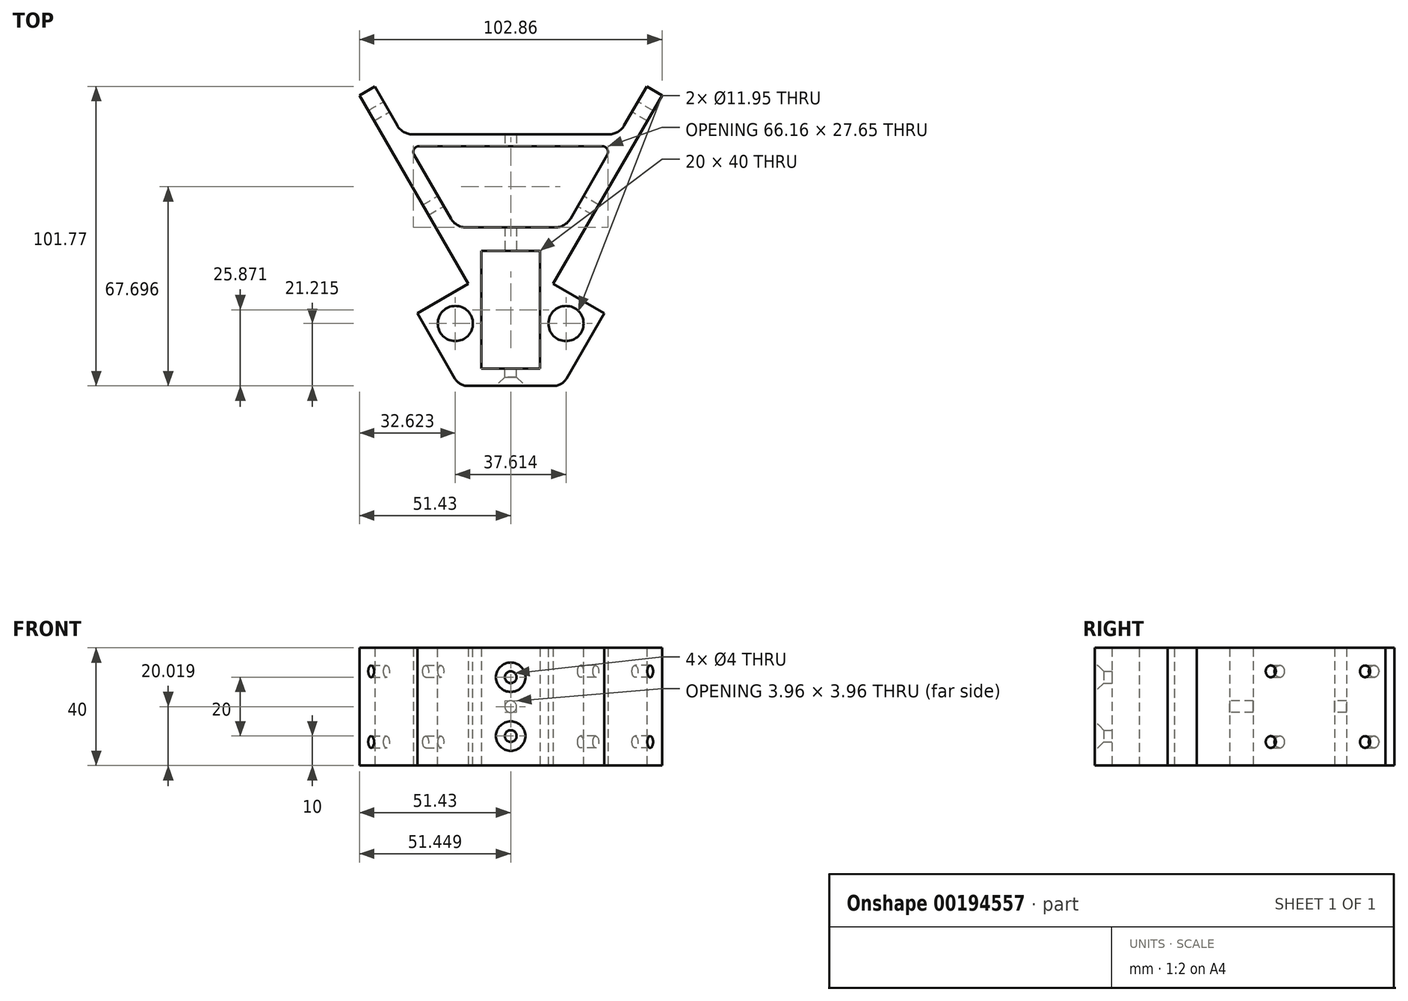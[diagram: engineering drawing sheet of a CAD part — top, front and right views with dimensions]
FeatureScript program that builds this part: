
annotation { "Feature Type Name" : "Feature", "Feature Type Description" : "" }
export const myFeature = defineFeature(function(context is Context, id is Id, definition is map)
    precondition{}
    {
        {
            var Q0;
            Q0=qCreatedBy(makeId("Top.planeOp"),FACE);
            var sketch = newSketch(context, id + "F0", { "sketchPlane" : qUnion([Q0])});
            skLineSegment(sketch, "E0", {"start": v(17.5, 30.31) * mm, "end": v(31.75, 55) * mm});
            skLineSegment(sketch, "E1", {"start": v(-17.5, 30.31) * mm, "end": v(-31.75, 55) * mm});
            skLineSegment(sketch, "E2", {"start": v(-17.5, 30.31) * mm, "end": v(17.5, 30.31) * mm});
            skLineSegment(sketch, "E3", {"start": v(-31.75, 55) * mm, "end": v(-14.43, 65) * mm});
            skLineSegment(sketch, "E4", {"start": v(-14.43, 65) * mm, "end": v(-51.43, 129.08) * mm});
            skLineSegment(sketch, "E5", {"start": v(-51.43, 129.08) * mm, "end": v(-46.23, 132.08) * mm});
            skLineSegment(sketch, "E6", {"start": v(31.75, 55) * mm, "end": v(14.43, 65) * mm});
            skLineSegment(sketch, "E7", {"start": v(14.43, 65) * mm, "end": v(51.43, 129.08) * mm});
            skLineSegment(sketch, "E8", {"start": v(51.43, 129.08) * mm, "end": v(46.23, 132.08) * mm});
            skLineSegment(sketch, "E9", {"start": v(-46.23, 132.08) * mm, "end": v(-36.85, 115.83) * mm});
            skLineSegment(sketch, "E10", {"start": v(18.58, 84.18) * mm, "end": v(34.54, 111.83) * mm});
            skLineSegment(sketch, "E11.bottom", {"start": v(-10, 36.18) * mm, "end": v(10, 36.18) * mm});
            skLineSegment(sketch, "E11.top", {"start": v(-10, 76.18) * mm, "end": v(10, 76.18) * mm});
            skLineSegment(sketch, "E11.left", {"start": v(-10, 36.18) * mm, "end": v(-10, 76.18) * mm});
            skLineSegment(sketch, "E11.right", {"start": v(10, 36.18) * mm, "end": v(10, 76.18) * mm});
            skLineSegment(sketch, "E12", {"start": v(36.85, 115.83) * mm, "end": v(-36.85, 115.83) * mm});
            skLineSegment(sketch, "E13.trimOffspring", {"start": v(36.85, 115.83) * mm, "end": v(46.23, 132.08) * mm});
            skLineSegment(sketch, "E14.trimOffspring", {"start": v(-34.54, 111.83) * mm, "end": v(-18.58, 84.18) * mm});
            skLineSegment(sketch, "E15", {"start": v(-34.54, 111.83) * mm, "end": v(34.54, 111.83) * mm});
            skLineSegment(sketch, "E16", {"start": v(18.58, 84.18) * mm, "end": v(-18.58, 84.18) * mm});
            skSolve(sketch);
        }
        {
            var Q0;
            Q0=qSketchRegion(id+"F0",true);
            extrude(context, id + "F1", {"entities" : qUnion([Q0]), "depth" : 40 * mm});
        }
        {
            var Q0;
            Q0=makeQuery(id+"F1.opExtrude","SWEPT_EDGE",EDGE,{"disambiguationData":[OSD([sQuery(id+"F0.wireOp",EDGE,"E1"),sQuery(id+"F0.wireOp",EDGE,"E2")])]});
            var Q1;
            Q1=makeQuery(id+"F1.opExtrude","SWEPT_EDGE",EDGE,{"disambiguationData":[OSD([sQuery(id+"F0.wireOp",EDGE,"E0"),sQuery(id+"F0.wireOp",EDGE,"E2")])]});
            fillet(context, id + "F2", {"entities" : qUnion([Q0, Q1]), "radius" : 5 * mm, "tangentPropagation" : true, "allowEdgeOverflow" : false});
        }
        {
            var Q0;
            Q0=makeQuery(id+"F1.opExtrude","SWEPT_EDGE",EDGE,{"disambiguationData":[OSD([sQuery(id+"F0.wireOp",EDGE,"E10"),sQuery(id+"F0.wireOp",EDGE,"E16")])]});
            var Q1;
            Q1=makeQuery(id+"F1.opExtrude","SWEPT_EDGE",EDGE,{"disambiguationData":[OSD([sQuery(id+"F0.wireOp",EDGE,"E14.trimOffspring"),sQuery(id+"F0.wireOp",EDGE,"E16")])]});
            var Q2;
            Q2=makeQuery(id+"F1.opExtrude","SWEPT_EDGE",EDGE,{"disambiguationData":[OSD([sQuery(id+"F0.wireOp",EDGE,"E9"),sQuery(id+"F0.wireOp",EDGE,"E12")])]});
            var Q3;
            Q3=makeQuery(id+"F1.opExtrude","SWEPT_EDGE",EDGE,{"disambiguationData":[OSD([sQuery(id+"F0.wireOp",EDGE,"E12"),sQuery(id+"F0.wireOp",EDGE,"E13.trimOffspring")])]});
            fillet(context, id + "F3", {"entities" : qUnion([Q0, Q1, Q2, Q3]), "radius" : 6 * mm, "tangentPropagation" : true, "allowEdgeOverflow" : false});
        }
        {
            var Q0;
            Q0=makeQuery(id+"F1.opExtrude","SWEPT_EDGE",EDGE,{"disambiguationData":[OSD([sQuery(id+"F0.wireOp",EDGE,"E10"),sQuery(id+"F0.wireOp",EDGE,"E15")])]});
            var Q1;
            Q1=makeQuery(id+"F1.opExtrude","SWEPT_EDGE",EDGE,{"disambiguationData":[OSD([sQuery(id+"F0.wireOp",EDGE,"E14.trimOffspring"),sQuery(id+"F0.wireOp",EDGE,"E15")])]});
            fillet(context, id + "F4", {"entities" : qUnion([Q0, Q1]), "radius" : 2 * mm, "tangentPropagation" : true, "allowEdgeOverflow" : false});
        }
        {
            var Q0;
            Q0=makeQuery(id+"F1.opExtrude","CAP_FACE",FACE,{"disambiguationData":[OSD([sQuery(id+"F0.wireOp",EDGE,"E0"),sQuery(id+"F0.wireOp",EDGE,"E1"),sQuery(id+"F0.wireOp",EDGE,"E2"),sQuery(id+"F0.wireOp",EDGE,"E3"),sQuery(id+"F0.wireOp",EDGE,"E4"),sQuery(id+"F0.wireOp",EDGE,"E5"),sQuery(id+"F0.wireOp",EDGE,"E6"),sQuery(id+"F0.wireOp",EDGE,"E7"),sQuery(id+"F0.wireOp",EDGE,"E8"),sQuery(id+"F0.wireOp",EDGE,"E9"),sQuery(id+"F0.wireOp",EDGE,"E10"),sQuery(id+"F0.wireOp",EDGE,"E11.bottom"),sQuery(id+"F0.wireOp",EDGE,"E11.top"),sQuery(id+"F0.wireOp",EDGE,"E11.left"),sQuery(id+"F0.wireOp",EDGE,"E11.right"),sQuery(id+"F0.wireOp",EDGE,"E12"),sQuery(id+"F0.wireOp",EDGE,"E13.trimOffspring"),sQuery(id+"F0.wireOp",EDGE,"E14.trimOffspring"),sQuery(id+"F0.wireOp",EDGE,"E15"),sQuery(id+"F0.wireOp",EDGE,"E16")])],"isStart":false});
            var sketch = newSketch(context, id + "F5", { "sketchPlane" : qUnion([Q0])});
            skCircle(sketch, "E17", {"center": v(-18.8, 51.52) * mm, "radius": 5.97 * mm});
            skCircle(sketch, "E18", {"center": v(18.8, 51.52) * mm, "radius": 5.97 * mm});
            skSolve(sketch);
        }
        {
            var Q0;
            Q0=qSketchRegion(id+"F5",true);
            extrude(context, id + "F6", {"entities" : qUnion([Q0]), "operationType" : NewBodyOperationType.REMOVE, "endBound" : BoundingType.THROUGH_ALL, "oppositeDirection" : true, "depth" : 25 * mm});
        }
        {
            var Q0;
            Q0=makeQuery(id+"F1.opExtrude","SWEPT_FACE",FACE,{"disambiguationData":[OSD([sQuery(id+"F0.wireOp",EDGE,"E12")])]});
            var sketch = newSketch(context, id + "F7", { "sketchPlane" : qUnion([Q0])});
            skPoint(sketch, "E19", {"position": v(0, 20) * mm});
            skPoint(sketch, "E19.positionSnap0", {"position": v(-33.39, 20) * mm});
            skSolve(sketch);
        }
        {
            var Q0;
            Q0=sQuery(id+"F7.wireOp",VERTEX,"E19");
            var Q1;
            Q1=makeQuery(id+"F1.opExtrude","SWEPT_BODY",BODY,{"disambiguationData":[OSD([sQuery(id+"F0.wireOp",EDGE,"E0"),sQuery(id+"F0.wireOp",EDGE,"E1"),sQuery(id+"F0.wireOp",EDGE,"E2"),sQuery(id+"F0.wireOp",EDGE,"E3"),sQuery(id+"F0.wireOp",EDGE,"E4"),sQuery(id+"F0.wireOp",EDGE,"E5"),sQuery(id+"F0.wireOp",EDGE,"E6"),sQuery(id+"F0.wireOp",EDGE,"E7"),sQuery(id+"F0.wireOp",EDGE,"E8"),sQuery(id+"F0.wireOp",EDGE,"E9"),sQuery(id+"F0.wireOp",EDGE,"E10"),sQuery(id+"F0.wireOp",EDGE,"E11.bottom"),sQuery(id+"F0.wireOp",EDGE,"E11.top"),sQuery(id+"F0.wireOp",EDGE,"E11.left"),sQuery(id+"F0.wireOp",EDGE,"E11.right"),sQuery(id+"F0.wireOp",EDGE,"E12"),sQuery(id+"F0.wireOp",EDGE,"E13.trimOffspring"),sQuery(id+"F0.wireOp",EDGE,"E14.trimOffspring"),sQuery(id+"F0.wireOp",EDGE,"E15"),sQuery(id+"F0.wireOp",EDGE,"E16")])]});
            hole(context, id + "F8", {"style" : HoleStyle.SIMPLE, "endStyle" : HoleEndStyle.BLIND, "holeDiameter" : 4 * mm, "holeDepth" : 40 * mm, "locations" : qUnion([Q0]), "scope" : qUnion([Q1]), "startStyle" : HoleStartStyle.PART});
        }
        {
            var Q0;
            Q0=makeQuery(id+"F1.opExtrude","SWEPT_FACE",FACE,{"disambiguationData":[OSD([sQuery(id+"F0.wireOp",EDGE,"E7")])]});
            var sketch = newSketch(context, id + "F9", { "sketchPlane" : qUnion([Q0])});
            skPoint(sketch, "E20", {"position": v(129.5, 32) * mm});
            skPoint(sketch, "E21", {"position": v(129.5, 8) * mm});
            skPoint(sketch, "E22", {"position": v(92.5, 8) * mm});
            skPoint(sketch, "E23", {"position": v(92.5, 32) * mm});
            skSolve(sketch);
        }
        {
            var Q0;
            Q0=sQuery(id+"F9.wireOp",VERTEX,"E20");
            var Q1;
            Q1=sQuery(id+"F9.wireOp",VERTEX,"E23");
            var Q2;
            Q2=sQuery(id+"F9.wireOp",VERTEX,"E22");
            var Q3;
            Q3=sQuery(id+"F9.wireOp",VERTEX,"E21");
            var Q4;
            Q4=makeQuery(id+"F1.opExtrude","SWEPT_BODY",BODY,{"disambiguationData":[OSD([sQuery(id+"F0.wireOp",EDGE,"E0"),sQuery(id+"F0.wireOp",EDGE,"E1"),sQuery(id+"F0.wireOp",EDGE,"E2"),sQuery(id+"F0.wireOp",EDGE,"E3"),sQuery(id+"F0.wireOp",EDGE,"E4"),sQuery(id+"F0.wireOp",EDGE,"E5"),sQuery(id+"F0.wireOp",EDGE,"E6"),sQuery(id+"F0.wireOp",EDGE,"E7"),sQuery(id+"F0.wireOp",EDGE,"E8"),sQuery(id+"F0.wireOp",EDGE,"E9"),sQuery(id+"F0.wireOp",EDGE,"E10"),sQuery(id+"F0.wireOp",EDGE,"E11.bottom"),sQuery(id+"F0.wireOp",EDGE,"E11.top"),sQuery(id+"F0.wireOp",EDGE,"E11.left"),sQuery(id+"F0.wireOp",EDGE,"E11.right"),sQuery(id+"F0.wireOp",EDGE,"E12"),sQuery(id+"F0.wireOp",EDGE,"E13.trimOffspring"),sQuery(id+"F0.wireOp",EDGE,"E14.trimOffspring"),sQuery(id+"F0.wireOp",EDGE,"E15"),sQuery(id+"F0.wireOp",EDGE,"E16")])]});
            hole(context, id + "F10", {"style" : HoleStyle.SIMPLE, "endStyle" : HoleEndStyle.BLIND, "holeDiameter" : 4 * mm, "holeDepth" : 12 * mm, "locations" : qUnion([Q0, Q1, Q2, Q3]), "scope" : qUnion([Q4]), "startStyle" : HoleStartStyle.PART});
        }
        {
            var Q0;
            Q0=makeQuery(id+"F1.opExtrude","SWEPT_FACE",FACE,{"disambiguationData":[OSD([sQuery(id+"F0.wireOp",EDGE,"E4")])]});
            var sketch = newSketch(context, id + "F11", { "sketchPlane" : qUnion([Q0])});
            skPoint(sketch, "E24", {"position": v(-129.5, 32) * mm});
            skPoint(sketch, "E25", {"position": v(-129.5, 8) * mm});
            skPoint(sketch, "E26", {"position": v(-92.5, 8) * mm});
            skPoint(sketch, "E27", {"position": v(-92.5, 32) * mm});
            skSolve(sketch);
        }
        {
            var Q0;
            Q0=sQuery(id+"F11.wireOp",VERTEX,"E24");
            var Q1;
            Q1=sQuery(id+"F11.wireOp",VERTEX,"E25");
            var Q2;
            Q2=sQuery(id+"F11.wireOp",VERTEX,"E26");
            var Q3;
            Q3=sQuery(id+"F11.wireOp",VERTEX,"E27");
            var Q4;
            Q4=makeQuery(id+"F1.opExtrude","SWEPT_BODY",BODY,{"disambiguationData":[OSD([sQuery(id+"F0.wireOp",EDGE,"E0"),sQuery(id+"F0.wireOp",EDGE,"E1"),sQuery(id+"F0.wireOp",EDGE,"E2"),sQuery(id+"F0.wireOp",EDGE,"E3"),sQuery(id+"F0.wireOp",EDGE,"E4"),sQuery(id+"F0.wireOp",EDGE,"E5"),sQuery(id+"F0.wireOp",EDGE,"E6"),sQuery(id+"F0.wireOp",EDGE,"E7"),sQuery(id+"F0.wireOp",EDGE,"E8"),sQuery(id+"F0.wireOp",EDGE,"E9"),sQuery(id+"F0.wireOp",EDGE,"E10"),sQuery(id+"F0.wireOp",EDGE,"E11.bottom"),sQuery(id+"F0.wireOp",EDGE,"E11.top"),sQuery(id+"F0.wireOp",EDGE,"E11.left"),sQuery(id+"F0.wireOp",EDGE,"E11.right"),sQuery(id+"F0.wireOp",EDGE,"E12"),sQuery(id+"F0.wireOp",EDGE,"E13.trimOffspring"),sQuery(id+"F0.wireOp",EDGE,"E14.trimOffspring"),sQuery(id+"F0.wireOp",EDGE,"E15"),sQuery(id+"F0.wireOp",EDGE,"E16")])]});
            hole(context, id + "F12", {"style" : HoleStyle.SIMPLE, "endStyle" : HoleEndStyle.BLIND, "holeDiameter" : 4 * mm, "holeDepth" : 12 * mm, "locations" : qUnion([Q0, Q1, Q2, Q3]), "scope" : qUnion([Q4]), "startStyle" : HoleStartStyle.PART});
        }
        {
            var Q0;
            Q0=makeQuery(id+"F1.opExtrude","SWEPT_FACE",FACE,{"disambiguationData":[OSD([sQuery(id+"F0.wireOp",EDGE,"E2")])]});
            var sketch = newSketch(context, id + "F13", { "sketchPlane" : qUnion([Q0])});
            skPoint(sketch, "E28", {"position": v(0, 30) * mm});
            skPoint(sketch, "E28.positionSnap0", {"position": v(0, 40) * mm});
            skPoint(sketch, "E29", {"position": v(0, 10) * mm});
            skPoint(sketch, "E29.positionSnap0", {"position": v(0, 0) * mm});
            skSolve(sketch);
        }
        {
            var Q0;
            Q0=sQuery(id+"F13.wireOp",VERTEX,"E28");
            var Q1;
            Q1=sQuery(id+"F13.wireOp",VERTEX,"E29");
            var Q2;
            Q2=makeQuery(id+"F1.opExtrude","SWEPT_BODY",BODY,{"disambiguationData":[OSD([sQuery(id+"F0.wireOp",EDGE,"E0"),sQuery(id+"F0.wireOp",EDGE,"E1"),sQuery(id+"F0.wireOp",EDGE,"E2"),sQuery(id+"F0.wireOp",EDGE,"E3"),sQuery(id+"F0.wireOp",EDGE,"E4"),sQuery(id+"F0.wireOp",EDGE,"E5"),sQuery(id+"F0.wireOp",EDGE,"E6"),sQuery(id+"F0.wireOp",EDGE,"E7"),sQuery(id+"F0.wireOp",EDGE,"E8"),sQuery(id+"F0.wireOp",EDGE,"E9"),sQuery(id+"F0.wireOp",EDGE,"E10"),sQuery(id+"F0.wireOp",EDGE,"E11.bottom"),sQuery(id+"F0.wireOp",EDGE,"E11.top"),sQuery(id+"F0.wireOp",EDGE,"E11.left"),sQuery(id+"F0.wireOp",EDGE,"E11.right"),sQuery(id+"F0.wireOp",EDGE,"E12"),sQuery(id+"F0.wireOp",EDGE,"E13.trimOffspring"),sQuery(id+"F0.wireOp",EDGE,"E14.trimOffspring"),sQuery(id+"F0.wireOp",EDGE,"E15"),sQuery(id+"F0.wireOp",EDGE,"E16")])]});
            hole(context, id + "F14", {"style" : HoleStyle.C_SINK, "endStyle" : HoleEndStyle.BLIND, "holeDiameter" : 4 * mm, "cSinkDiameter" : 10 * mm, "cSinkAngle" : 90 * degree, "holeDepth" : 12 * mm, "locations" : qUnion([Q0, Q1]), "scope" : qUnion([Q2]), "startStyle" : HoleStartStyle.PART});
        }
    });
